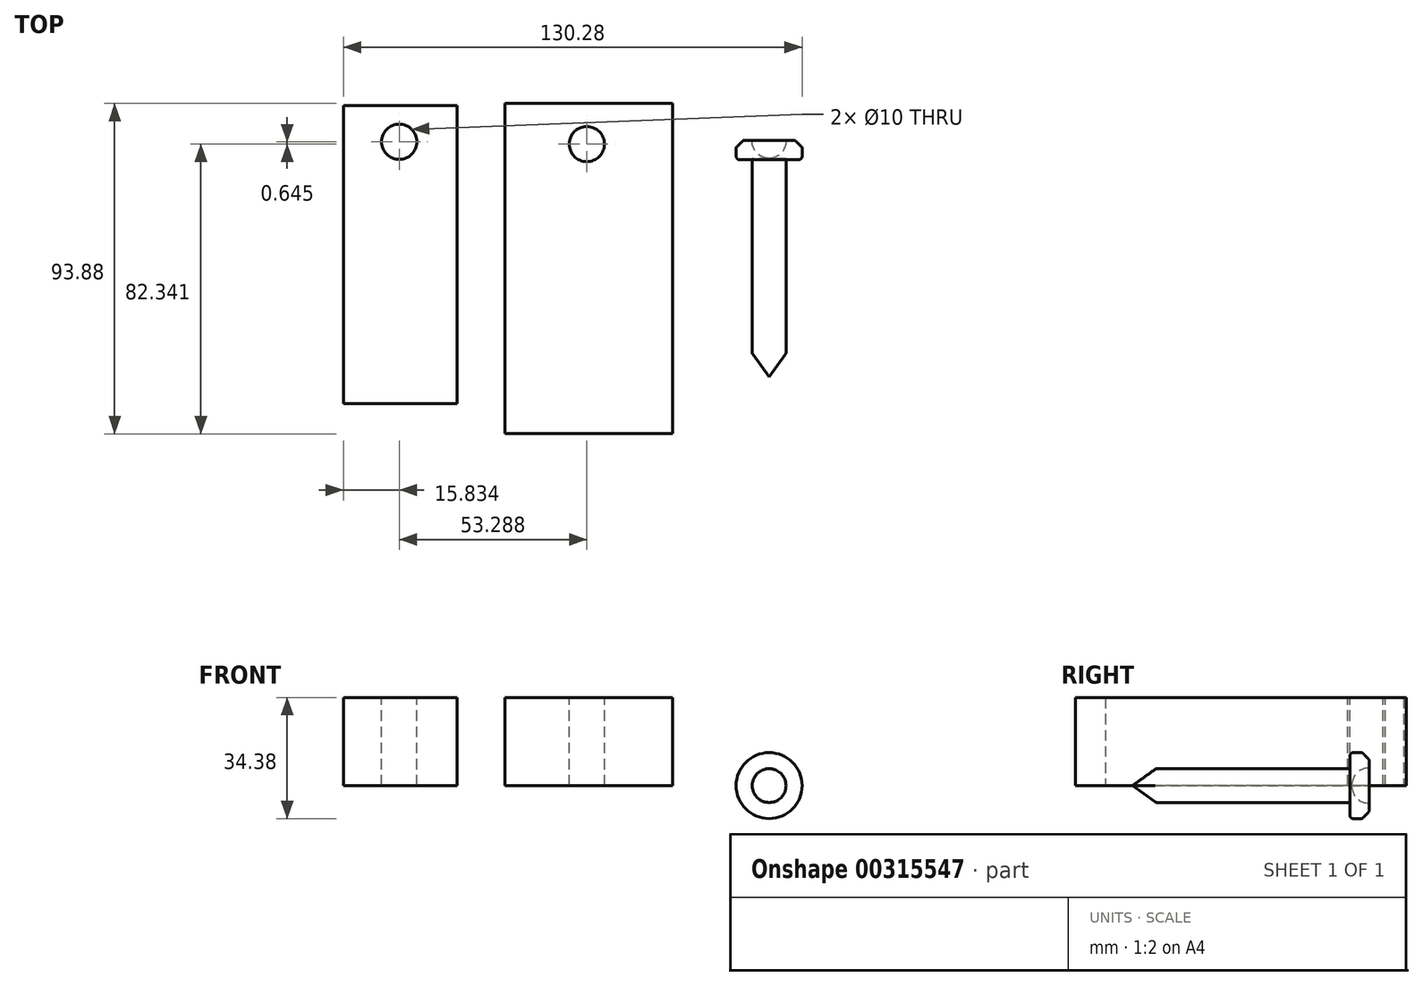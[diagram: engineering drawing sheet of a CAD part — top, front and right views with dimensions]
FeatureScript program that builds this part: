
annotation { "Feature Type Name" : "Feature", "Feature Type Description" : "" }
export const myFeature = defineFeature(function(context is Context, id is Id, definition is map)
    precondition{}
    {
        {
            var Q0;
            Q0=qCreatedBy(makeId("Top.planeOp"),FACE);
            var sketch = newSketch(context, id + "F0", { "sketchPlane" : qUnion([Q0])});
            skLineSegment(sketch, "E0.bottom", {"start": v(-31.87, -21.5) * mm, "end": v(-64.18, -21.5) * mm});
            skLineSegment(sketch, "E0.top", {"start": v(-31.87, 63.2) * mm, "end": v(-64.18, 63.2) * mm});
            skLineSegment(sketch, "E0.left", {"start": v(-31.87, -21.5) * mm, "end": v(-31.87, 63.2) * mm});
            skLineSegment(sketch, "E0.right", {"start": v(-64.18, -21.5) * mm, "end": v(-64.18, 63.2) * mm});
            skPoint(sketch, "E0.middle", {"position": v(-48.03, 20.85) * mm});
            skSolve(sketch);
        }
        {
            var Q0;
            Q0=qCreatedBy(makeId("Top.planeOp"),FACE);
            var sketch = newSketch(context, id + "F1", { "sketchPlane" : qUnion([Q0])});
            skLineSegment(sketch, "E1.bottom", {"start": v(29.25, 63.86) * mm, "end": v(-18.34, 63.86) * mm});
            skLineSegment(sketch, "E1.top", {"start": v(29.25, -30.02) * mm, "end": v(-18.34, -30.02) * mm});
            skLineSegment(sketch, "E1.left", {"start": v(29.25, 63.86) * mm, "end": v(29.25, -30.02) * mm});
            skLineSegment(sketch, "E1.right", {"start": v(-18.34, 63.86) * mm, "end": v(-18.34, -30.02) * mm});
            skPoint(sketch, "E1.middle", {"position": v(5.46, 16.92) * mm});
            skSolve(sketch);
        }
        {
            var Q0;
            Q0=makeQuery(id+"F0.imprint","IMPRINT",FACE,{"disambiguationData":[TD([[makeQuery(id+"F0.imprint","IMPRINT",EDGE,{"derivedFrom":sQuery(id+"F0.wireOp",EDGE,"E0.bottom")}),-1.0]])]});
            extrude(context, id + "F2", {"entities" : qUnion([Q0]), "depth" : 25 * mm});
        }
        {
            var Q0;
            Q0=makeQuery(id+"F1.imprint","IMPRINT",FACE,{"disambiguationData":[TD([[makeQuery(id+"F1.imprint","IMPRINT",EDGE,{"derivedFrom":sQuery(id+"F1.wireOp",EDGE,"E1.bottom")}),1.0]])]});
            extrude(context, id + "F3", {"entities" : qUnion([Q0]), "depth" : 25 * mm});
        }
        {
            var Q0;
            Q0=makeQuery(id+"F2.opExtrude","CAP_FACE",FACE,{"disambiguationData":[OSD([sQuery(id+"F0.wireOp",EDGE,"E0.bottom"),sQuery(id+"F0.wireOp",EDGE,"E0.top"),sQuery(id+"F0.wireOp",EDGE,"E0.left"),sQuery(id+"F0.wireOp",EDGE,"E0.right")])],"isStart":false});
            var sketch = newSketch(context, id + "F4", { "sketchPlane" : qUnion([Q0])});
            skCircle(sketch, "E2", {"center": v(-48.35, 52.97) * mm, "radius": 5 * mm});
            skSolve(sketch);
        }
        {
            var Q0;
            Q0 = qSketchRegion(id + "F4", true);
            extrude(context, id + "F5", {"entities" : qUnion([Q0]), "operationType" : NewBodyOperationType.REMOVE, "oppositeDirection" : true, "depth" : 30 * mm});
        }
        {
            var Q0;
            Q0=makeQuery(id+"F3.opExtrude","CAP_FACE",FACE,{"disambiguationData":[OSD([sQuery(id+"F1.wireOp",EDGE,"E1.bottom"),sQuery(id+"F1.wireOp",EDGE,"E1.top"),sQuery(id+"F1.wireOp",EDGE,"E1.left"),sQuery(id+"F1.wireOp",EDGE,"E1.right")])],"isStart":false});
            var sketch = newSketch(context, id + "F6", { "sketchPlane" : qUnion([Q0])});
            skCircle(sketch, "E3", {"center": v(4.94, 52.32) * mm, "radius": 5 * mm});
            skSolve(sketch);
        }
        {
            var Q0;
            Q0 = qSketchRegion(id + "F6", true);
            extrude(context, id + "F7", {"entities" : qUnion([Q0]), "operationType" : NewBodyOperationType.REMOVE, "oppositeDirection" : true, "depth" : 30 * mm});
        }
        {
            var Q0;
            Q0=qCreatedBy(makeId("Top.planeOp"),FACE);
            var sketch = newSketch(context, id + "F8", { "sketchPlane" : qUnion([Q0])});
            skCircle(sketch, "E4", {"center": v(56.73, 53.4) * mm, "radius": 5 * mm});
            skLineSegment(sketch, "E5", {"start": v(56.73, 53.4) * mm, "end": v(64.03, 53.4) * mm});
            skLineSegment(sketch, "E6", {"start": v(64.03, 53.4) * mm, "end": v(66.1, 51.45) * mm});
            skLineSegment(sketch, "E7", {"start": v(66.1, 51.45) * mm, "end": v(66.1, 47.8) * mm});
            skLineSegment(sketch, "E8", {"start": v(66.1, 47.8) * mm, "end": v(61.52, 48.1) * mm});
            skLineSegment(sketch, "E9", {"start": v(61.52, 48.1) * mm, "end": v(61.52, -7.2) * mm});
            skLineSegment(sketch, "E10", {"start": v(61.52, -7.2) * mm, "end": v(56.73, -13.86) * mm});
            skLineSegment(sketch, "E11", {"start": v(56.73, -13.86) * mm, "end": v(56.73, 53.4) * mm});
            skSolve(sketch);
        }
        {
            var Q0;
            {var subQ0=sQuery(id+"F8.wireOp",EDGE,"E6");Q0=makeQuery(id+"F8.imprint","IMPRINT",FACE,{"disambiguationData":[TD([[makeQuery(id+"F8.imprint","IMPRINT",EDGE,{"derivedFrom":subQ0}),-1.0]])]});}
            var Q1;
            Q1=sQuery(id+"F8.wireOp",EDGE,"E11");
            revolve(context, id + "F9", {"entities" : qUnion([Q0]), "axis" : qUnion([Q1]), "revolveType" : RevolveType.FULL});
        }
        {
            var Q0;
            Q0=makeQuery(id+"F9.opRevolve","SWEPT_EDGE",EDGE,{"disambiguationData":[OSD([sQuery(id+"F8.wireOp",EDGE,"E6"),sQuery(id+"F8.wireOp",EDGE,"E7")])]});
            var Q1;
            Q1=makeQuery(id+"F9.opRevolve","SWEPT_EDGE",EDGE,{"disambiguationData":[OSD([sQuery(id+"F8.wireOp",EDGE,"E5"),sQuery(id+"F8.wireOp",EDGE,"E6")])]});
            var Q2;
            Q2=makeQuery(id+"F9.opRevolve","SWEPT_EDGE",EDGE,{"disambiguationData":[OSD([sQuery(id+"F8.wireOp",EDGE,"E7"),sQuery(id+"F8.wireOp",EDGE,"E8")])]});
            var Q3;
            Q3=makeQuery(id+"F9.opRevolve","SWEPT_EDGE",EDGE,{"disambiguationData":[OSD([sQuery(id+"F8.wireOp",EDGE,"E9"),sQuery(id+"F8.wireOp",EDGE,"E10")])]});
            fillet(context, id + "F10", {"entities" : qUnion([Q0, Q1, Q2, Q3]), "radius" : 1 * mm, "tangentPropagation" : true, "allowEdgeOverflow" : false});
        }
    });
